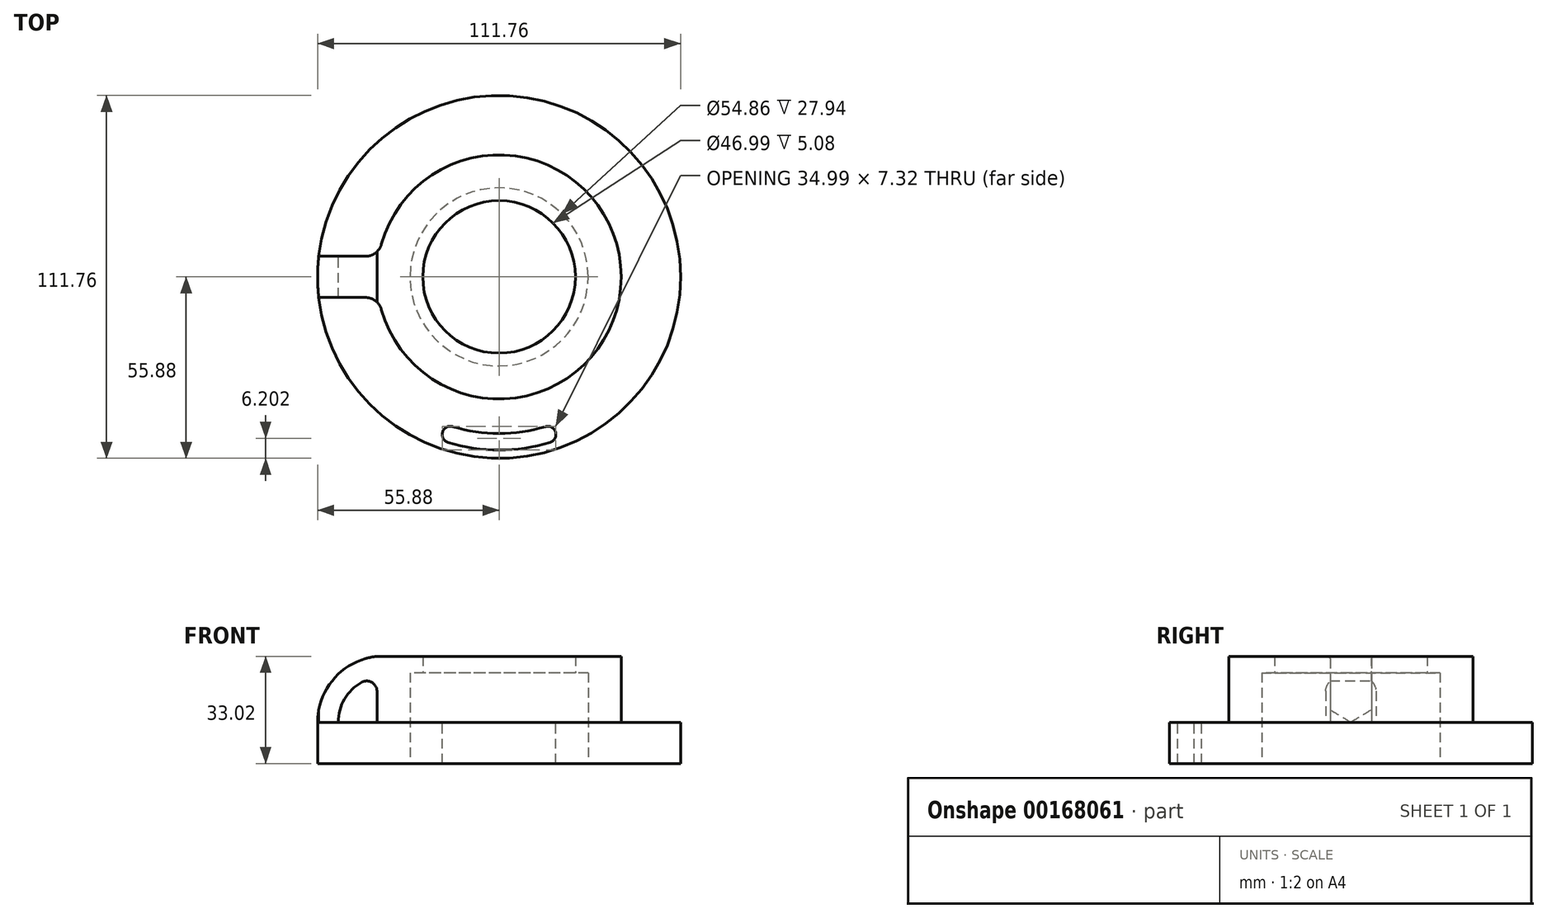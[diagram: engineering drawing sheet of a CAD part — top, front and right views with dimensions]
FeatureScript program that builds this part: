
annotation { "Feature Type Name" : "Feature", "Feature Type Description" : "" }
export const myFeature = defineFeature(function(context is Context, id is Id, definition is map)
    precondition{}
    {
        {
            var Q0;
            Q0=qCreatedBy(makeId("Top.planeOp"),FACE);
            var sketch = newSketch(context, id + "F0", { "sketchPlane" : qUnion([Q0])});
            skCircle(sketch, "E0", {"center": v(0, 0) * mm, "radius": 55.88 * mm});
            skCircle(sketch, "E1", {"center": v(0, 0) * mm, "radius": 27.43 * mm});
            skSolve(sketch);
        }
        {
            var Q0;
            Q0 = qSketchRegion(id + "F0", true);
            extrude(context, id + "F1", {"entities" : qUnion([Q0]), "depth" : 12.7 * mm});
        }
        {
            var Q0;
            Q0=makeQuery(id+"F1.opExtrude","CAP_FACE",FACE,{"disambiguationData":[OSD([sQuery(id+"F0.wireOp",EDGE,"E0"),sQuery(id+"F0.wireOp",EDGE,"E1")])],"isStart":false});
            var sketch = newSketch(context, id + "F2", { "sketchPlane" : qUnion([Q0])});
            skCircle(sketch, "E2", {"center": v(0, 0) * mm, "radius": 37.6 * mm});
            skCircle(sketch, "E3", {"center": v(0, 0) * mm, "radius": 27.43 * mm});
            skSolve(sketch);
        }
        {
            var Q0;
            Q0 = qSketchRegion(id + "F2", true);
            extrude(context, id + "F3", {"entities" : qUnion([Q0]), "operationType" : NewBodyOperationType.ADD, "depth" : 15.24 * mm});
        }
        {
            var Q0;
            Q0=makeQuery(id+"F3.opExtrude","CAP_FACE",FACE,{"disambiguationData":[OSD([sQuery(id+"F2.wireOp",EDGE,"E2"),sQuery(id+"F2.wireOp",EDGE,"E3")])],"isStart":false});
            var sketch = newSketch(context, id + "F4", { "sketchPlane" : qUnion([Q0])});
            skCircle(sketch, "E4.0", {"center": v(0, 0) * mm, "radius": 37.6 * mm});
            skCircle(sketch, "E5", {"center": v(0, 0) * mm, "radius": 23.5 * mm});
            skSolve(sketch);
        }
        {
            var Q0;
            Q0 = qSketchRegion(id + "F4", true);
            extrude(context, id + "F5", {"entities" : qUnion([Q0]), "operationType" : NewBodyOperationType.ADD, "depth" : 5.08 * mm});
        }
        {
            var Q0;
            Q0=makeQuery(id+"F1.opExtrude","CAP_FACE",FACE,{"disambiguationData":[OSD([sQuery(id+"F0.wireOp",EDGE,"E0"),sQuery(id+"F0.wireOp",EDGE,"E1")])],"isStart":false});
            var sketch = newSketch(context, id + "F6", { "sketchPlane" : qUnion([Q0])});
            skArc(sketch, "E6", {"start": v(17.37, -47.74) * mm, "mid": v(0, -50.8) * mm, "end": v(-17.37, -47.74) * mm, "construction": true});
            skLineSegment(sketch, "E7", {"start": v(-17.37, -47.74) * mm, "end": v(0, 0) * mm, "construction": true});
            skLineSegment(sketch, "E8", {"start": v(17.37, -47.74) * mm, "end": v(0, 0) * mm, "construction": true});
            skArc(sketch, "E9", {"start": v(-16.5, -45.35) * mm, "mid": v(0, -48.26) * mm, "end": v(16.5, -45.35) * mm});
            skArc(sketch, "E10", {"start": v(-18.24, -50.12) * mm, "mid": v(0, -53.34) * mm, "end": v(18.24, -50.12) * mm});
            skLineSegment(sketch, "E11", {"start": v(-18.24, -50.12) * mm, "end": v(-17.37, -47.74) * mm, "construction": true});
            skLineSegment(sketch, "E12", {"start": v(18.24, -50.12) * mm, "end": v(17.37, -47.74) * mm, "construction": true});
            skLineSegment(sketch, "E13", {"start": v(16.5, -45.35) * mm, "end": v(18.24, -50.12) * mm});
            skLineSegment(sketch, "E14", {"start": v(-18.24, -50.12) * mm, "end": v(-16.5, -45.35) * mm});
            skSolve(sketch);
        }
        {
            var Q0;
            Q0 = qSketchRegion(id + "F6", true);
            extrude(context, id + "F7", {"entities" : qUnion([Q0]), "operationType" : NewBodyOperationType.REMOVE, "endBound" : BoundingType.THROUGH_ALL, "oppositeDirection" : true, "depth" : 25.4 * mm});
        }
        {
            var Q0;
            Q0=makeQuery(id+"F7.boolean.opBoolean","COPY",EDGE,{"derivedFrom":makeQuery(id+"F7.opExtrude","SWEPT_EDGE",EDGE,{"disambiguationData":[OSD([sQuery(id+"F6.wireOp",EDGE,"E10"),sQuery(id+"F6.wireOp",EDGE,"E14")])]})});
            var Q1;
            Q1=makeQuery(id+"F7.boolean.opBoolean","COPY",EDGE,{"derivedFrom":makeQuery(id+"F7.opExtrude","SWEPT_EDGE",EDGE,{"disambiguationData":[OSD([sQuery(id+"F6.wireOp",EDGE,"E9"),sQuery(id+"F6.wireOp",EDGE,"E14")])]})});
            var Q2;
            Q2=makeQuery(id+"F7.boolean.opBoolean","COPY",EDGE,{"derivedFrom":makeQuery(id+"F7.opExtrude","SWEPT_EDGE",EDGE,{"disambiguationData":[OSD([sQuery(id+"F6.wireOp",EDGE,"E10"),sQuery(id+"F6.wireOp",EDGE,"E13")])]})});
            var Q3;
            Q3=makeQuery(id+"F7.boolean.opBoolean","COPY",EDGE,{"derivedFrom":makeQuery(id+"F7.opExtrude","SWEPT_EDGE",EDGE,{"disambiguationData":[OSD([sQuery(id+"F6.wireOp",EDGE,"E9"),sQuery(id+"F6.wireOp",EDGE,"E13")])]})});
            fillet(context, id + "F8", {"entities" : qUnion([Q0, Q1, Q2, Q3]), "radius" : 2.54 * mm, "tangentPropagation" : true, "allowEdgeOverflow" : false});
        }
        {
            var Q0;
            Q0=qCreatedBy(makeId("Front.planeOp"),FACE);
            var sketch = newSketch(context, id + "F9", { "sketchPlane" : qUnion([Q0])});
            skLineSegment(sketch, "E15.0", {"start": v(-55.88, 12.7) * mm, "end": v(55.88, 12.7) * mm, "construction": true});
            skLineSegment(sketch, "E16.0", {"start": v(-37.6, 33.02) * mm, "end": v(37.6, 33.02) * mm, "construction": true});
            skLineSegment(sketch, "E17", {"start": v(-49.53, 12.7) * mm, "end": v(-55.88, 12.7) * mm, "construction": true});
            skArc(sketch, "E18", {"start": v(-37.6, 33.02) * mm, "mid": v(-50.63, 26.37) * mm, "end": v(-55.88, 12.7) * mm});
            skLineSegment(sketch, "E19", {"start": v(-37.6, 33.02) * mm, "end": v(-37.6, 26.67) * mm, "construction": true});
            skArc(sketch, "E20", {"start": v(-37.6, 26.67) * mm, "mid": v(-46.14, 21.89) * mm, "end": v(-49.53, 12.7) * mm});
            skLineSegment(sketch, "E21", {"start": v(-55.88, 12.7) * mm, "end": v(-55.88, 10.16) * mm});
            skLineSegment(sketch, "E22", {"start": v(-55.88, 10.16) * mm, "end": v(-49.53, 10.16) * mm});
            skLineSegment(sketch, "E23", {"start": v(-49.53, 10.16) * mm, "end": v(-49.53, 12.7) * mm, "construction": true});
            skLineSegment(sketch, "E24", {"start": v(-37.6, 33.02) * mm, "end": v(-35.05, 33.02) * mm});
            skLineSegment(sketch, "E25", {"start": v(-35.05, 33.02) * mm, "end": v(-35.05, 26.67) * mm});
            skLineSegment(sketch, "E26", {"start": v(-35.05, 26.67) * mm, "end": v(-37.6, 26.67) * mm});
            skLineSegment(sketch, "E27", {"start": v(-37.6, 26.67) * mm, "end": v(-35.05, 26.67) * mm});
            skLineSegment(sketch, "E28", {"start": v(-49.53, 12.7) * mm, "end": v(-37.6, 12.7) * mm});
            skLineSegment(sketch, "E29", {"start": v(-37.6, 12.7) * mm, "end": v(-37.6, 26.67) * mm});
            skLineSegment(sketch, "E30", {"start": v(-49.53, 10.16) * mm, "end": v(-33.8, 10.16) * mm});
            skLineSegment(sketch, "E31", {"start": v(-33.8, 10.16) * mm, "end": v(-35.05, 26.67) * mm});
            skSolve(sketch);
        }
        {
            var Q0;
            Q0 = qSketchRegion(id + "F9", true);
            extrude(context, id + "F10", {"entities" : qUnion([Q0]), "operationType" : NewBodyOperationType.ADD, "depth" : 6.35 * mm, "hasSecondDirection" : true, "secondDirectionOppositeDirection" : true, "secondDirectionDepth" : 6.35 * mm});
        }
        {
            var Q0;
            Q0=makeQuery(id+"F10.opExtrude","SWEPT_EDGE",EDGE,{"disambiguationData":[OSD([sQuery(id+"F9.wireOp",EDGE,"E20"),sQuery(id+"F9.wireOp",EDGE,"E23")])]});
            var Q1;
            Q1=makeQuery(id+"F10.opExtrude","SWEPT_EDGE",EDGE,{"disambiguationData":[OSD([sQuery(id+"F9.wireOp",EDGE,"E28"),sQuery(id+"F9.wireOp",EDGE,"E29")])]});
            fillet(context, id + "F11", {"entities" : qUnion([Q0, Q1]), "radius" : 3.17 * mm, "tangentPropagation" : true, "allowEdgeOverflow" : false});
        }
        {
            var Q0;
            Q0=makeQuery(id+"F10.boolean.opBoolean","INTERSECT",EDGE,{"derivedFrom":[makeQuery(id+"F5.boolean.opBoolean","MERGE",FACE,{"derivedFrom":[makeQuery(id+"F3.opExtrude","SWEPT_FACE",FACE,{"disambiguationData":[OSD([sQuery(id+"F2.wireOp",EDGE,"E2")])]}),makeQuery(id+"F5.opExtrude","SWEPT_FACE",FACE,{"disambiguationData":[OSD([sQuery(id+"F4.wireOp",EDGE,"E4.0")])]})]}),makeQuery(id+"F10.opExtrude","CAP_FACE",FACE,{"disambiguationData":[OSD([sQuery(id+"F9.wireOp",EDGE,"E18"),sQuery(id+"F9.wireOp",EDGE,"E20"),sQuery(id+"F9.wireOp",EDGE,"E21"),sQuery(id+"F9.wireOp",EDGE,"E22"),sQuery(id+"F9.wireOp",EDGE,"E23"),sQuery(id+"F9.wireOp",EDGE,"E24"),sQuery(id+"F9.wireOp",EDGE,"E25"),sQuery(id+"F9.wireOp",EDGE,"E27")])],"isStart":false})]});
            var Q1;
            Q1=makeQuery(id+"F10.boolean.opBoolean","INTERSECT",EDGE,{"derivedFrom":[makeQuery(id+"F5.boolean.opBoolean","MERGE",FACE,{"derivedFrom":[makeQuery(id+"F3.opExtrude","SWEPT_FACE",FACE,{"disambiguationData":[OSD([sQuery(id+"F2.wireOp",EDGE,"E2")])]}),makeQuery(id+"F5.opExtrude","SWEPT_FACE",FACE,{"disambiguationData":[OSD([sQuery(id+"F4.wireOp",EDGE,"E4.0")])]})]}),makeQuery(id+"F10.opExtrude","CAP_FACE",FACE,{"disambiguationData":[OSD([sQuery(id+"F9.wireOp",EDGE,"E18"),sQuery(id+"F9.wireOp",EDGE,"E20"),sQuery(id+"F9.wireOp",EDGE,"E21"),sQuery(id+"F9.wireOp",EDGE,"E22"),sQuery(id+"F9.wireOp",EDGE,"E23"),sQuery(id+"F9.wireOp",EDGE,"E24"),sQuery(id+"F9.wireOp",EDGE,"E25"),sQuery(id+"F9.wireOp",EDGE,"E27")])],"isStart":true})]});
            fillet(context, id + "F12", {"entities" : qUnion([Q0, Q1]), "radius" : 5.08 * mm, "tangentPropagation" : true, "allowEdgeOverflow" : false});
        }
        {
            var Q0;
            Q0=makeQuery(id+"F1.opExtrude","CAP_FACE",FACE,{"disambiguationData":[OSD([sQuery(id+"F0.wireOp",EDGE,"E0"),sQuery(id+"F0.wireOp",EDGE,"E1")])],"isStart":true});
            var sketch = newSketch(context, id + "F13", { "sketchPlane" : qUnion([Q0])});
            skCircle(sketch, "E32.0", {"center": v(0, 0) * mm, "radius": 55.88 * mm});
            skCircle(sketch, "E33.0", {"center": v(0, 0) * mm, "radius": 62.23 * mm});
            skSolve(sketch);
        }
        {
            var Q0;
            Q0 = qSketchRegion(id + "F13", true);
            extrude(context, id + "F14", {"entities" : qUnion([Q0]), "operationType" : NewBodyOperationType.REMOVE, "endBound" : BoundingType.THROUGH_ALL, "oppositeDirection" : true, "depth" : 25.4 * mm});
        }
    });
